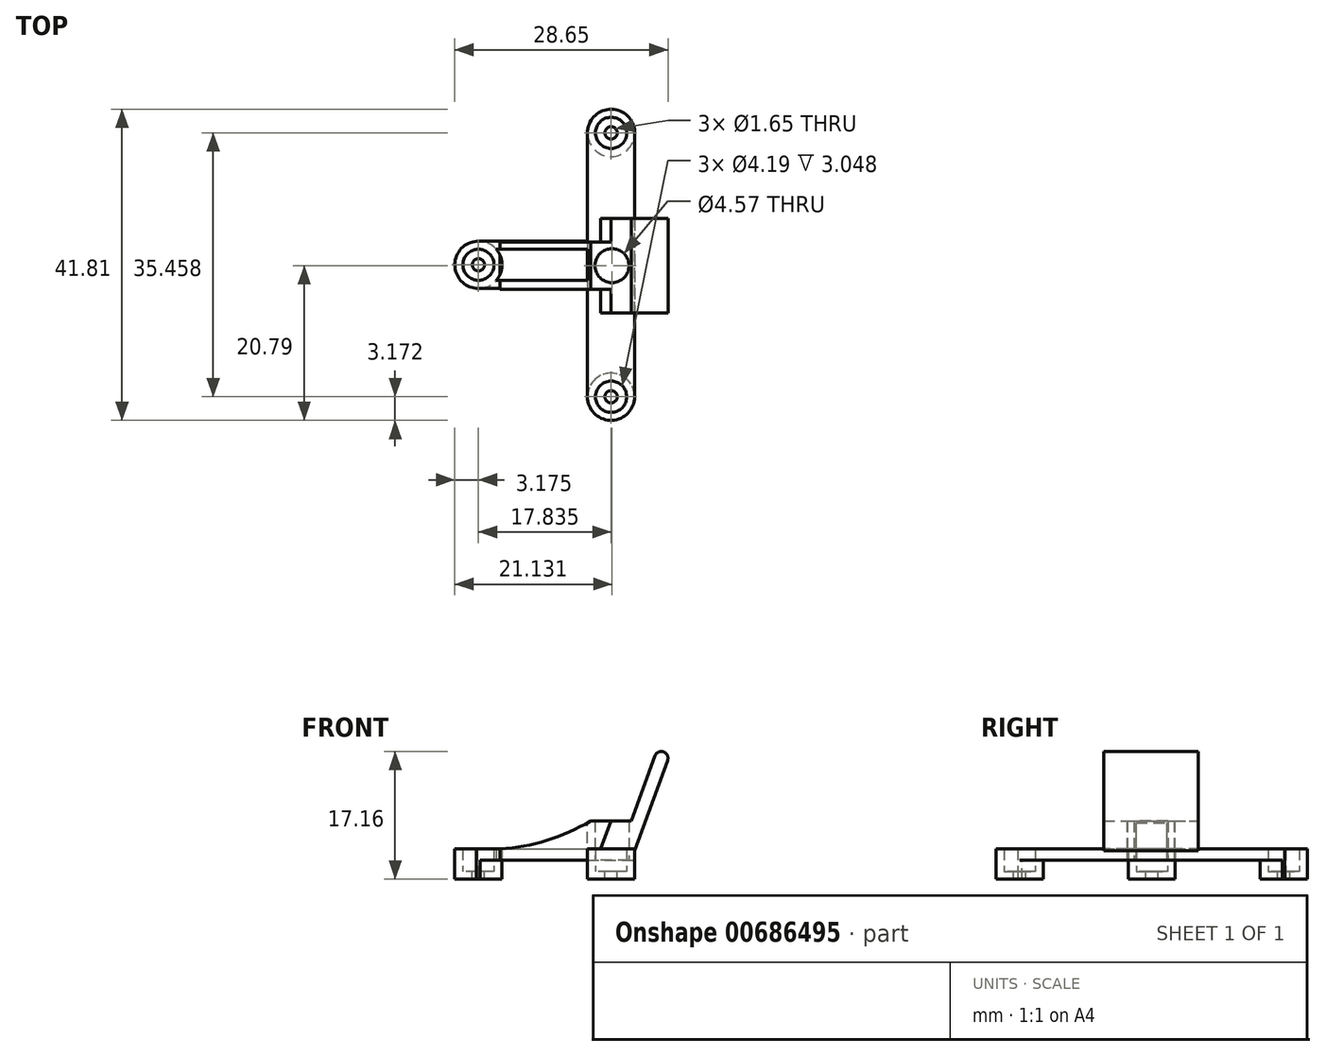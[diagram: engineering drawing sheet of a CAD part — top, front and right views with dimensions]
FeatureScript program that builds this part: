
annotation { "Feature Type Name" : "Feature", "Feature Type Description" : "" }
export const myFeature = defineFeature(function(context is Context, id is Id, definition is map)
    precondition{}
    {
        {
            var Q0;
            Q0=qCreatedBy(makeId("Top.planeOp"),FACE);
            var sketch = newSketch(context, id + "F0", { "sketchPlane" : qUnion([Q0])});
            skCircle(sketch, "E0", {"center": v(-9.68, 0.11) * mm, "radius": 3.18 * mm});
            skCircle(sketch, "E1", {"center": v(8.16, -17.62) * mm, "radius": 3.18 * mm});
            skCircle(sketch, "E2", {"center": v(8.16, 17.84) * mm, "radius": 3.18 * mm});
            skCircle(sketch, "E3", {"center": v(8.16, 17.84) * mm, "radius": 2.1 * mm});
            skCircle(sketch, "E4", {"center": v(8.16, -17.62) * mm, "radius": 2.1 * mm});
            skCircle(sketch, "E5", {"center": v(-9.68, 0.11) * mm, "radius": 2.1 * mm});
            skLineSegment(sketch, "E6", {"start": v(11.33, 18) * mm, "end": v(11.33, -17.62) * mm});
            skLineSegment(sketch, "E7", {"start": v(5, 18.1) * mm, "end": v(5, -17.92) * mm});
            skCircle(sketch, "E8", {"center": v(8.16, 17.84) * mm, "radius": 0.83 * mm});
            skCircle(sketch, "E9", {"center": v(8.16, -17.62) * mm, "radius": 0.83 * mm});
            skCircle(sketch, "E10", {"center": v(-9.68, 0.11) * mm, "radius": 0.83 * mm});
            skLineSegment(sketch, "E11", {"start": v(-9.93, -3.05) * mm, "end": v(5, -3.05) * mm});
            skLineSegment(sketch, "E12", {"start": v(-9.85, 3.28) * mm, "end": v(5, 3.28) * mm});
            skLineSegment(sketch, "E13.trimOffspring", {"start": v(-7.28, -1.97) * mm, "end": v(5, -1.97) * mm});
            skLineSegment(sketch, "E14.trimOffspring", {"start": v(-7.28, 2.2) * mm, "end": v(5, 2.2) * mm});
            skPoint(sketch, "E15.start.orphan", {"position": v(-9.85, 2.2) * mm});
            skPoint(sketch, "E16.start.orphan", {"position": v(-9.93, -1.97) * mm});
            skCircle(sketch, "E17", {"center": v(8.28, 0) * mm, "radius": 2.29 * mm});
            skLineSegment(sketch, "E18", {"start": v(8.16, 17.84) * mm, "end": v(8.16, -17.62) * mm, "construction": true});
            skSolve(sketch);
        }
        {
            var Q0;
            Q0=qCreatedBy(makeId("Front.planeOp"),FACE);
            var sketch = newSketch(context, id + "F1", { "sketchPlane" : qUnion([Q0])});
            skLineSegment(sketch, "E19", {"start": v(5.38, 5.27) * mm, "end": v(10.86, 5.27) * mm});
            skLineSegment(sketch, "E20", {"start": v(10.86, 5.27) * mm, "end": v(14.6, 15.54) * mm});
            skLineSegment(sketch, "E21", {"start": v(15.75, 13.41) * mm, "end": v(10.86, 0) * mm});
            skLineSegment(sketch, "E22", {"start": v(5.06, 0) * mm, "end": v(10.86, 0) * mm});
            skLineSegment(sketch, "E23", {"start": v(5.06, 0) * mm, "end": v(-9.95, 0) * mm});
            skLineSegment(sketch, "E24", {"start": v(-6.76, 0) * mm, "end": v(-6.76, 1.52) * mm});
            skLineSegment(sketch, "E25", {"start": v(-6.76, 0) * mm, "end": v(10.86, 0) * mm});
            skLineSegment(sketch, "E26", {"start": v(8.12, 5.27) * mm, "end": v(6.2, 0) * mm});
            skArc(sketch, "E27", {"start": v(15.75, 13.41) * mm, "mid": v(15.2, 14.57) * mm, "end": v(14.05, 14.03) * mm});
            skPoint(sketch, "E28", {"position": v(14.6, 15.54) * mm});
            skArc(sketch, "E29", {"start": v(-6.76, 1.52) * mm, "mid": v(-0.47, 2.68) * mm, "end": v(5.38, 5.27) * mm});
            skSolve(sketch);
        }
        {
            var Q0;
            {var subQ4=sQuery(id+"F0.wireOp",EDGE,"E6");var subQ5=sQuery(id+"F0.wireOp",EDGE,"E1");var subQ6=makeQuery(id+"F0.imprint","INTERSECT",VERTEX,{"derivedFrom":[subQ5,subQ4]});Q0=makeQuery(id+"F0.imprint","IMPRINT",FACE,{"disambiguationData":[TD([[makeQuery(id+"F0.imprint","IMPRINT",EDGE,{"disambiguationData":[TD([[subQ6,-1.0]])],"derivedFrom":subQ5}),-1.0]])]});}
            var Q1;
            Q1=makeQuery(id+"F0.imprint","IMPRINT",FACE,{"disambiguationData":[TD([[makeQuery(id+"F0.imprint","IMPRINT",EDGE,{"derivedFrom":sQuery(id+"F0.wireOp",EDGE,"E3")}),-1.0]])]});
            var Q2;
            Q2=makeQuery(id+"F0.imprint","IMPRINT",FACE,{"disambiguationData":[TD([[makeQuery(id+"F0.imprint","IMPRINT",EDGE,{"derivedFrom":sQuery(id+"F0.wireOp",EDGE,"E4")}),-1.0]])]});
            var Q3;
            Q3=makeQuery(id+"F0.imprint","IMPRINT",FACE,{"disambiguationData":[TD([[makeQuery(id+"F0.imprint","IMPRINT",EDGE,{"derivedFrom":sQuery(id+"F0.wireOp",EDGE,"E5")}),-1.0]])]});
            extrude(context, id + "F2", {"entities" : qUnion([Q0, Q1, Q2, Q3]), "depth" : 1.52 * mm, "offsetDistance" : 25.4 * mm});
        }
        {
            var Q0;
            {var subQ1=sQuery(id+"F1.wireOp",EDGE,"E20");Q0=makeQuery(id+"F1.imprint","IMPRINT",FACE,{"disambiguationData":[TD([[makeQuery(id+"F1.imprint","IMPRINT",EDGE,{"derivedFrom":subQ1}),-1.0]])]});}
            extrude(context, id + "F3", {"entities" : qUnion([Q0]), "operationType" : NewBodyOperationType.ADD, "endBound" : BoundingType.SYMMETRIC, "depth" : 12.7 * mm, "offsetDistance" : 25.4 * mm});
        }
        {
            var Q0;
            {var subQ1=sQuery(id+"F1.wireOp",EDGE,"E24");Q0=makeQuery(id+"F1.imprint","IMPRINT",FACE,{"disambiguationData":[TD([[makeQuery(id+"F1.imprint","IMPRINT",EDGE,{"derivedFrom":subQ1}),-1.0]])]});}
            extrude(context, id + "F4", {"entities" : qUnion([Q0]), "operationType" : NewBodyOperationType.ADD, "endBound" : BoundingType.SYMMETRIC, "depth" : 6.35 * mm, "offsetDistance" : 25.4 * mm});
        }
        {
            var Q0;
            {var subQ0=sQuery(id+"F0.wireOp",EDGE,"E14.trimOffspring");Q0=makeQuery(id+"F0.imprint","IMPRINT",FACE,{"disambiguationData":[TD([[makeQuery(id+"F0.imprint","IMPRINT",EDGE,{"derivedFrom":subQ0}),1.0]])]});}
            var Q1;
            {var subQ0=sQuery(id+"F0.wireOp",EDGE,"E13.trimOffspring");Q1=makeQuery(id+"F0.imprint","IMPRINT",FACE,{"disambiguationData":[TD([[makeQuery(id+"F0.imprint","IMPRINT",EDGE,{"derivedFrom":subQ0}),-1.0]])]});}
            extrude(context, id + "F5", {"entities" : qUnion([Q0, Q1]), "depth" : 1.52 * mm, "offsetDistance" : 25.4 * mm});
        }
        {
            var Q0;
            {var subQ0=sQuery(id+"F0.wireOp",EDGE,"E13.trimOffspring");Q0=makeQuery(id+"F0.imprint","IMPRINT",FACE,{"disambiguationData":[TD([[makeQuery(id+"F0.imprint","IMPRINT",EDGE,{"derivedFrom":subQ0}),1.0]])]});}
            extrude(context, id + "F6", {"entities" : qUnion([Q0]), "operationType" : NewBodyOperationType.REMOVE, "endBound" : BoundingType.SYMMETRIC, "oppositeDirection" : true, "depth" : 25.4 * mm, "offsetDistance" : 25.4 * mm});
        }
        {
            var Q0;
            Q0=makeQuery(id+"F0.imprint","IMPRINT",FACE,{"disambiguationData":[TD([[makeQuery(id+"F0.imprint","IMPRINT",EDGE,{"derivedFrom":sQuery(id+"F0.wireOp",EDGE,"E4")}),-1.0]])]});
            var Q1;
            Q1=makeQuery(id+"F0.imprint","IMPRINT",FACE,{"disambiguationData":[TD([[makeQuery(id+"F0.imprint","IMPRINT",EDGE,{"derivedFrom":sQuery(id+"F0.wireOp",EDGE,"E4")}),1.0]])]});
            extrude(context, id + "F7", {"entities" : qUnion([Q0, Q1]), "operationType" : NewBodyOperationType.ADD, "oppositeDirection" : true, "depth" : 2.54 * mm, "offsetDistance" : 25.4 * mm});
        }
        {
            var Q0;
            Q0=makeQuery(id+"F0.imprint","IMPRINT",FACE,{"disambiguationData":[TD([[makeQuery(id+"F0.imprint","IMPRINT",EDGE,{"derivedFrom":sQuery(id+"F0.wireOp",EDGE,"E4")}),1.0]])]});
            extrude(context, id + "F8", {"entities" : qUnion([Q0]), "operationType" : NewBodyOperationType.REMOVE, "oppositeDirection" : true, "depth" : 1.52 * mm, "offsetDistance" : 25.4 * mm});
        }
        {
            var Q0;
            Q0=makeQuery(id+"F0.imprint","IMPRINT",FACE,{"disambiguationData":[TD([[makeQuery(id+"F0.imprint","IMPRINT",EDGE,{"derivedFrom":sQuery(id+"F0.wireOp",EDGE,"E5")}),-1.0]])]});
            var Q1;
            Q1=makeQuery(id+"F0.imprint","IMPRINT",FACE,{"disambiguationData":[TD([[makeQuery(id+"F0.imprint","IMPRINT",EDGE,{"derivedFrom":sQuery(id+"F0.wireOp",EDGE,"E5")}),1.0]])]});
            extrude(context, id + "F9", {"entities" : qUnion([Q0, Q1]), "operationType" : NewBodyOperationType.ADD, "oppositeDirection" : true, "depth" : 2.54 * mm, "offsetDistance" : 25.4 * mm});
        }
        {
            var Q0;
            Q0=makeQuery(id+"F0.imprint","IMPRINT",FACE,{"disambiguationData":[TD([[makeQuery(id+"F0.imprint","IMPRINT",EDGE,{"derivedFrom":sQuery(id+"F0.wireOp",EDGE,"E5")}),1.0]])]});
            extrude(context, id + "F10", {"entities" : qUnion([Q0]), "operationType" : NewBodyOperationType.REMOVE, "oppositeDirection" : true, "depth" : 1.52 * mm, "offsetDistance" : 25.4 * mm});
        }
        {
            var Q0;
            Q0=makeQuery(id+"F0.imprint","IMPRINT",FACE,{"disambiguationData":[TD([[makeQuery(id+"F0.imprint","IMPRINT",EDGE,{"derivedFrom":sQuery(id+"F0.wireOp",EDGE,"E3")}),-1.0]])]});
            var Q1;
            Q1=makeQuery(id+"F0.imprint","IMPRINT",FACE,{"disambiguationData":[TD([[makeQuery(id+"F0.imprint","IMPRINT",EDGE,{"derivedFrom":sQuery(id+"F0.wireOp",EDGE,"E3")}),1.0]])]});
            extrude(context, id + "F11", {"entities" : qUnion([Q0, Q1]), "operationType" : NewBodyOperationType.ADD, "oppositeDirection" : true, "depth" : 2.54 * mm, "offsetDistance" : 25.4 * mm});
        }
        {
            var Q0;
            Q0=makeQuery(id+"F0.imprint","IMPRINT",FACE,{"disambiguationData":[TD([[makeQuery(id+"F0.imprint","IMPRINT",EDGE,{"derivedFrom":sQuery(id+"F0.wireOp",EDGE,"E3")}),1.0]])]});
            extrude(context, id + "F12", {"entities" : qUnion([Q0]), "operationType" : NewBodyOperationType.REMOVE, "oppositeDirection" : true, "depth" : 1.52 * mm, "offsetDistance" : 25.4 * mm});
        }
        {
            var Q0;
            Q0=makeQuery(id+"F0.imprint","IMPRINT",FACE,{"disambiguationData":[TD([[makeQuery(id+"F0.imprint","IMPRINT",EDGE,{"derivedFrom":sQuery(id+"F0.wireOp",EDGE,"E17")}),1.0]])]});
            extrude(context, id + "F13", {"entities" : qUnion([Q0]), "operationType" : NewBodyOperationType.REMOVE, "depth" : 25.4 * mm, "offsetDistance" : 25.4 * mm});
        }
    });
